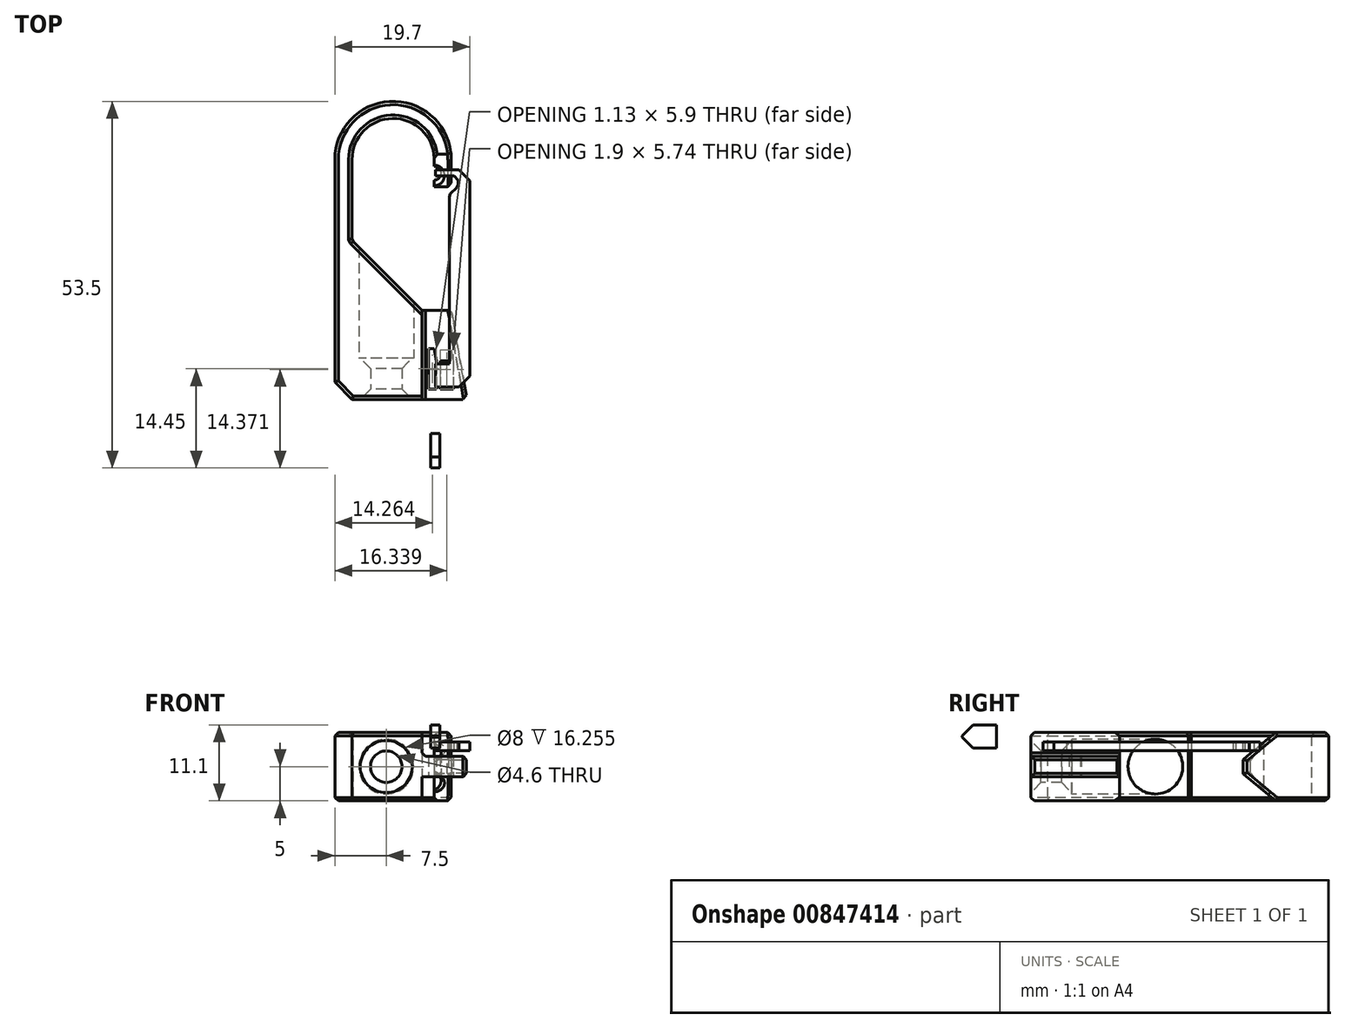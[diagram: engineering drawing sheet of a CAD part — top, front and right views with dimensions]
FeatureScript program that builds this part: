
annotation { "Feature Type Name" : "Feature", "Feature Type Description" : "" }
export const myFeature = defineFeature(function(context is Context, id is Id, definition is map)
    precondition{}
    {
        {
            var Q0;
            Q0=qCreatedBy(makeId("Top.planeOp"),FACE);
            var sketch = newSketch(context, id + "F0", { "sketchPlane" : qUnion([Q0])});
            skCircle(sketch, "E0", {"center": v(-1, -1.5) * mm, "radius": 4 * mm});
            skLineSegment(sketch, "E1.bottom", {"start": v(-8.5, 3.5) * mm, "end": v(8.5, 3.5) * mm});
            skLineSegment(sketch, "E1.top", {"start": v(-8.5, -6.5) * mm, "end": v(8.5, -6.5) * mm});
            skLineSegment(sketch, "E1.left", {"start": v(-8.5, 3.5) * mm, "end": v(-8.5, -6.5) * mm});
            skLineSegment(sketch, "E1.right", {"start": v(8.5, 3.5) * mm, "end": v(8.5, -6.5) * mm});
            skPoint(sketch, "E1.middle", {"position": v(0, -1.5) * mm});
            skCircle(sketch, "E2", {"center": v(-1, -1.5) * mm, "radius": 2.3 * mm});
            skSolve(sketch);
        }
        {
            var Q0;
            Q0=qCreatedBy(makeId("Front.planeOp"),FACE);
            cPlane(context, id + "F1", {"entities" : qUnion([Q0]), "cplaneType" : CPlaneType.OFFSET, "offset" : 3.5 * mm, "oppositeDirection" : true, "width" : 150 * mm, "height" : 150 * mm});
        }
        {
            var Q0;
            Q0=qCreatedBy(id+"F1.planeOp",FACE);
            var sketch = newSketch(context, id + "F2", { "sketchPlane" : qUnion([Q0])});
            skLineSegment(sketch, "E3", {"start": v(0, 0) * mm, "end": v(8.5, 0) * mm});
            skLineSegment(sketch, "E4.MirrorCS", {"start": v(0, 0) * mm, "end": v(-8.5, 0) * mm});
            skLineSegment(sketch, "E5", {"start": v(8.5, 0) * mm, "end": v(8.5, 13) * mm});
            skLineSegment(sketch, "E6", {"start": v(8.5, 13) * mm, "end": v(4.2, 13) * mm});
            skLineSegment(sketch, "E7", {"start": v(4.2, 13) * mm, "end": v(-6, 23.2) * mm});
            skLineSegment(sketch, "E8", {"start": v(-8.5, 0) * mm, "end": v(-8.5, 35) * mm});
            skLineSegment(sketch, "E9", {"start": v(-6, 23.2) * mm, "end": v(-6, 35) * mm});
            skLineSegment(sketch, "E10", {"start": v(-6, 35) * mm, "end": v(0, 35) * mm});
            skArc(sketch, "E11", {"start": v(8.5, 35) * mm, "mid": v(0, 43.5) * mm, "end": v(-8.5, 35) * mm});
            skArc(sketch, "E12", {"start": v(6, 35) * mm, "mid": v(0, 41) * mm, "end": v(-6, 35) * mm});
            skLineSegment(sketch, "E13", {"start": v(0, 35) * mm, "end": v(8.5, 35) * mm});
            skLineSegment(sketch, "E14", {"start": v(6, 35) * mm, "end": v(6, 31) * mm});
            skLineSegment(sketch, "E15.bottom", {"start": v(6, 31) * mm, "end": v(8.5, 31) * mm});
            skLineSegment(sketch, "E15.top", {"start": v(6, 35) * mm, "end": v(8.5, 35) * mm});
            skLineSegment(sketch, "E15.left", {"start": v(6, 31) * mm, "end": v(6, 35) * mm});
            skLineSegment(sketch, "E15.right", {"start": v(8.5, 31) * mm, "end": v(8.5, 35) * mm});
            skLineSegment(sketch, "E16", {"start": v(8.5, 13) * mm, "end": v(10.8, 0) * mm});
            skLineSegment(sketch, "E17", {"start": v(10.8, 0) * mm, "end": v(8.5, 0) * mm});
            skLineSegment(sketch, "E18", {"start": v(4.2, 13) * mm, "end": v(4.2, 0) * mm});
            skLineSegment(sketch, "E19.0", {"start": v(5.2, 12) * mm, "end": v(5.2, 0) * mm});
            skLineSegment(sketch, "E19.1", {"start": v(7.66, 12) * mm, "end": v(5.2, 12) * mm});
            skLineSegment(sketch, "E19.2", {"start": v(7.66, 12) * mm, "end": v(9.6, 1) * mm});
            skLineSegment(sketch, "E19.3", {"start": v(9.6, 1) * mm, "end": v(8.5, 1) * mm});
            skLineSegment(sketch, "E20", {"start": v(8.5, 1) * mm, "end": v(5.2, 1) * mm});
            skLineSegment(sketch, "E21", {"start": v(5.2, 12) * mm, "end": v(7.14, 1) * mm});
            skCircle(sketch, "E22", {"center": v(6, 33) * mm, "radius": 1 * mm});
            skLineSegment(sketch, "E23.0", {"start": v(8.5, 11.5) * mm, "end": v(4.2, 11.5) * mm});
            skLineSegment(sketch, "E24.0", {"start": v(0, 1.5) * mm, "end": v(8.5, 1.5) * mm});
            skLineSegment(sketch, "E24.1", {"start": v(10.8, 1.5) * mm, "end": v(8.5, 1.5) * mm});
            skLineSegment(sketch, "E25", {"start": v(8.79, 5.6) * mm, "end": v(8.79, 1) * mm});
            skLineSegment(sketch, "E26", {"start": v(8.79, 5.6) * mm, "end": v(6.33, 5.6) * mm});
            skLineSegment(sketch, "E27", {"start": v(7.66, 12) * mm, "end": v(7.66, 7.4) * mm});
            skLineSegment(sketch, "E28", {"start": v(7.66, 7.4) * mm, "end": v(5.2, 7.4) * mm});
            skLineSegment(sketch, "E29", {"start": v(6.33, 5.6) * mm, "end": v(6.33, 1) * mm});
            skLineSegment(sketch, "E30", {"start": v(8.79, 5.6) * mm, "end": v(6.89, 5.6) * mm});
            skLineSegment(sketch, "E31", {"start": v(6.89, 5.6) * mm, "end": v(6.89, 1) * mm});
            skLineSegment(sketch, "E32", {"start": v(5.2, 7.4) * mm, "end": v(7.1, 7.4) * mm});
            skLineSegment(sketch, "E33", {"start": v(7.1, 7.4) * mm, "end": v(7.1, 12) * mm});
            skSolve(sketch);
        }
        {
            var Q0;
            {var subQ0=sQuery(id+"F2.wireOp",EDGE,"E20");var subQ1=sQuery(id+"F2.wireOp",EDGE,"E19.0");var subQ2=makeQuery(id+"F2.imprint","INTERSECT",VERTEX,{"derivedFrom":[subQ1,subQ0]});Q0=makeQuery(id+"F2.imprint","IMPRINT",FACE,{"disambiguationData":[TD([[makeQuery(id+"F2.imprint","IMPRINT",EDGE,{"disambiguationData":[TD([[subQ2,1.0]])],"derivedFrom":subQ1}),1.0]])]});}
            var Q1;
            {var subQ1=sQuery(id+"F2.wireOp",EDGE,"E6");Q1=makeQuery(id+"F2.imprint","IMPRINT",FACE,{"disambiguationData":[TD([[makeQuery(id+"F2.imprint","IMPRINT",EDGE,{"derivedFrom":subQ1}),1.0]])]});}
            var Q2;
            {var subQ4=sQuery(id+"F2.wireOp",EDGE,"E23.0");var subQ5=sQuery(id+"F2.wireOp",EDGE,"E18");var subQ6=makeQuery(id+"F2.imprint","INTERSECT",VERTEX,{"derivedFrom":[subQ5,subQ4]});Q2=makeQuery(id+"F2.imprint","IMPRINT",FACE,{"disambiguationData":[TD([[makeQuery(id+"F2.imprint","IMPRINT",EDGE,{"disambiguationData":[TD([[subQ6,-1.0]])],"derivedFrom":subQ5}),1.0]])]});}
            var Q3;
            {var subQ4=sQuery(id+"F2.wireOp",EDGE,"E3");var subQ6=sQuery(id+"F2.wireOp",EDGE,"E18");var subQ7=makeQuery(id+"F2.imprint","INTERSECT",VERTEX,{"derivedFrom":[subQ4,subQ6]});Q3=makeQuery(id+"F2.imprint","IMPRINT",FACE,{"disambiguationData":[TD([[makeQuery(id+"F2.imprint","IMPRINT",EDGE,{"disambiguationData":[TD([[subQ7,-1.0]])],"derivedFrom":subQ4}),1.0]])]});}
            var Q4;
            {var subQ4=sQuery(id+"F2.wireOp",EDGE,"E19.0");var subQ5=sQuery(id+"F2.wireOp",EDGE,"E3");var subQ6=makeQuery(id+"F2.imprint","INTERSECT",VERTEX,{"derivedFrom":[subQ5,subQ4]});Q4=makeQuery(id+"F2.imprint","IMPRINT",FACE,{"disambiguationData":[TD([[makeQuery(id+"F2.imprint","IMPRINT",EDGE,{"disambiguationData":[TD([[subQ6,1.0]])],"derivedFrom":subQ4}),1.0]])]});}
            var Q5;
            {var subQ5=sQuery(id+"F2.wireOp",EDGE,"E17");Q5=makeQuery(id+"F2.imprint","IMPRINT",FACE,{"disambiguationData":[TD([[makeQuery(id+"F2.imprint","IMPRINT",EDGE,{"derivedFrom":subQ5}),-1.0]])]});}
            var Q6;
            {var subQ2=sQuery(id+"F2.wireOp",EDGE,"E5");var subQ8=makeQuery(id+"F2.imprint","INTERSECT",VERTEX,{"derivedFrom":[subQ2,sQuery(id+"F2.wireOp",EDGE,"E23.0")]});Q6=makeQuery(id+"F2.imprint","IMPRINT",FACE,{"disambiguationData":[TD([[makeQuery(id+"F2.imprint","IMPRINT",EDGE,{"disambiguationData":[TD([[subQ8,1.0]])],"derivedFrom":subQ2}),-1.0]])]});}
            var Q7;
            {var subQ4=sQuery(id+"F2.wireOp",EDGE,"E4.MirrorCS");Q7=makeQuery(id+"F2.imprint","IMPRINT",FACE,{"disambiguationData":[TD([[makeQuery(id+"F2.imprint","IMPRINT",EDGE,{"derivedFrom":subQ4}),-1.0]])]});}
            var Q8;
            {var subQ0=sQuery(id+"F2.wireOp",EDGE,"E23.0");var subQ1=sQuery(id+"F2.wireOp",EDGE,"E5");var subQ2=makeQuery(id+"F2.imprint","INTERSECT",VERTEX,{"derivedFrom":[subQ1,subQ0]});Q8=makeQuery(id+"F2.imprint","IMPRINT",FACE,{"disambiguationData":[TD([[makeQuery(id+"F2.imprint","IMPRINT",EDGE,{"disambiguationData":[TD([[subQ2,1.0]])],"derivedFrom":subQ1}),1.0]])]});}
            var Q9;
            {var subQ1=sQuery(id+"F2.wireOp",EDGE,"E19.2");var subQ3=sQuery(id+"F2.wireOp",EDGE,"E23.0");var subQ4=makeQuery(id+"F2.imprint","INTERSECT",VERTEX,{"derivedFrom":[subQ1,subQ3]});Q9=makeQuery(id+"F2.imprint","IMPRINT",FACE,{"disambiguationData":[TD([[makeQuery(id+"F2.imprint","IMPRINT",EDGE,{"disambiguationData":[TD([[subQ4,-1.0]])],"derivedFrom":subQ3}),-1.0]])]});}
            var Q10;
            {var subQ5=sQuery(id+"F2.wireOp",EDGE,"E15.bottom");Q10=makeQuery(id+"F2.imprint","IMPRINT",FACE,{"disambiguationData":[TD([[makeQuery(id+"F2.imprint","IMPRINT",EDGE,{"derivedFrom":subQ5}),1.0]])]});}
            var Q11;
            {var subQ1=sQuery(id+"F2.wireOp",EDGE,"E19.2");var subQ3=sQuery(id+"F2.wireOp",EDGE,"E24.1");var subQ4=makeQuery(id+"F2.imprint","INTERSECT",VERTEX,{"derivedFrom":[subQ1,subQ3]});Q11=makeQuery(id+"F2.imprint","IMPRINT",FACE,{"disambiguationData":[TD([[makeQuery(id+"F2.imprint","IMPRINT",EDGE,{"disambiguationData":[TD([[subQ4,-1.0]])],"derivedFrom":subQ3}),-1.0]])]});}
            var Q12;
            {var subQ0=sQuery(id+"F2.wireOp",EDGE,"E19.3");var subQ1=sQuery(id+"F2.wireOp",EDGE,"E19.2");var subQ2=makeQuery(id+"F2.imprint","INTERSECT",VERTEX,{"derivedFrom":[subQ1,subQ0]});Q12=makeQuery(id+"F2.imprint","IMPRINT",FACE,{"disambiguationData":[TD([[makeQuery(id+"F2.imprint","IMPRINT",EDGE,{"disambiguationData":[TD([[subQ2,1.0]])],"derivedFrom":subQ1}),-1.0]])]});}
            var Q13;
            {var subQ0=sQuery(id+"F2.wireOp",EDGE,"E21");var subQ1=sQuery(id+"F2.wireOp",EDGE,"E20");var subQ2=makeQuery(id+"F2.imprint","INTERSECT",VERTEX,{"derivedFrom":[subQ1,subQ0]});Q13=makeQuery(id+"F2.imprint","IMPRINT",FACE,{"disambiguationData":[TD([[makeQuery(id+"F2.imprint","IMPRINT",EDGE,{"disambiguationData":[TD([[subQ2,-1.0]])],"derivedFrom":subQ1}),-1.0]])]});}
            var Q14;
            {var subQ0=sQuery(id+"F2.wireOp",EDGE,"E20");var subQ5=sQuery(id+"F2.wireOp",EDGE,"E21");var subQ6=makeQuery(id+"F2.imprint","INTERSECT",VERTEX,{"derivedFrom":[subQ0,subQ5]});Q14=makeQuery(id+"F2.imprint","IMPRINT",FACE,{"disambiguationData":[TD([[makeQuery(id+"F2.imprint","IMPRINT",EDGE,{"disambiguationData":[TD([[subQ6,1.0]])],"derivedFrom":subQ5}),1.0]])]});}
            var Q15;
            {var subQ0=sQuery(id+"F2.wireOp",EDGE,"E19.3");var subQ5=sQuery(id+"F2.wireOp",EDGE,"E25");var subQ6=makeQuery(id+"F2.imprint","INTERSECT",VERTEX,{"derivedFrom":[subQ0,subQ5]});Q15=makeQuery(id+"F2.imprint","IMPRINT",FACE,{"disambiguationData":[TD([[makeQuery(id+"F2.imprint","IMPRINT",EDGE,{"disambiguationData":[TD([[subQ6,1.0]])],"derivedFrom":subQ5}),-1.0]])]});}
            var Q16;
            {var subQ0=sQuery(id+"F2.wireOp",EDGE,"E27");var subQ5=sQuery(id+"F2.wireOp",EDGE,"E23.0");var subQ6=makeQuery(id+"F2.imprint","INTERSECT",VERTEX,{"derivedFrom":[subQ5,subQ0]});Q16=makeQuery(id+"F2.imprint","IMPRINT",FACE,{"disambiguationData":[TD([[makeQuery(id+"F2.imprint","IMPRINT",EDGE,{"disambiguationData":[TD([[subQ6,-1.0]])],"derivedFrom":subQ5}),-1.0]])]});}
            var Q17;
            {var subQ0=sQuery(id+"F2.wireOp",EDGE,"E21");var subQ5=sQuery(id+"F2.wireOp",EDGE,"E23.0");var subQ7=makeQuery(id+"F2.imprint","INTERSECT",VERTEX,{"derivedFrom":[subQ0,subQ5]});Q17=makeQuery(id+"F2.imprint","IMPRINT",FACE,{"disambiguationData":[TD([[makeQuery(id+"F2.imprint","IMPRINT",EDGE,{"disambiguationData":[TD([[subQ7,1.0]])],"derivedFrom":subQ5}),-1.0]])]});}
            var Q18;
            {var subQ1=sQuery(id+"F2.wireOp",EDGE,"E19.0");var subQ3=sQuery(id+"F2.wireOp",EDGE,"E23.0");var subQ4=makeQuery(id+"F2.imprint","INTERSECT",VERTEX,{"derivedFrom":[subQ1,subQ3]});Q18=makeQuery(id+"F2.imprint","IMPRINT",FACE,{"disambiguationData":[TD([[makeQuery(id+"F2.imprint","IMPRINT",EDGE,{"disambiguationData":[TD([[subQ4,1.0]])],"derivedFrom":subQ3}),-1.0]])]});}
            var Q19;
            {var subQ5=sQuery(id+"F2.wireOp",EDGE,"E28");Q19=makeQuery(id+"F2.imprint","IMPRINT",FACE,{"disambiguationData":[TD([[makeQuery(id+"F2.imprint","IMPRINT",EDGE,{"derivedFrom":subQ5}),-1.0]])]});}
            var Q20;
            {var subQ0=sQuery(id+"F2.wireOp",EDGE,"E26");Q20=makeQuery(id+"F2.imprint","IMPRINT",FACE,{"disambiguationData":[TD([[makeQuery(id+"F2.imprint","IMPRINT",EDGE,{"derivedFrom":subQ0}),-1.0]])]});}
            var Q21;
            {var subQ5=sQuery(id+"F2.wireOp",EDGE,"E32");var subQ6=sQuery(id+"F2.wireOp",EDGE,"E19.0");var subQ7=makeQuery(id+"F2.imprint","INTERSECT",VERTEX,{"derivedFrom":[subQ6,subQ5]});Q21=makeQuery(id+"F2.imprint","IMPRINT",FACE,{"disambiguationData":[TD([[makeQuery(id+"F2.imprint","IMPRINT",EDGE,{"disambiguationData":[TD([[subQ7,-1.0]])],"derivedFrom":subQ6}),1.0]])]});}
            var Q22;
            {var subQ0=sQuery(id+"F2.wireOp",EDGE,"E26");Q22=makeQuery(id+"F2.imprint","IMPRINT",FACE,{"disambiguationData":[TD([[makeQuery(id+"F2.imprint","IMPRINT",EDGE,{"derivedFrom":subQ0}),1.0]])]});}
            var Q23;
            {var subQ0=sQuery(id+"F2.wireOp",EDGE,"E29");var subQ5=sQuery(id+"F2.wireOp",EDGE,"E24.0");var subQ6=makeQuery(id+"F2.imprint","INTERSECT",VERTEX,{"derivedFrom":[subQ5,subQ0]});Q23=makeQuery(id+"F2.imprint","IMPRINT",FACE,{"disambiguationData":[TD([[makeQuery(id+"F2.imprint","IMPRINT",EDGE,{"disambiguationData":[TD([[subQ6,-1.0]])],"derivedFrom":subQ5}),1.0]])]});}
            var Q24;
            {var subQ0=sQuery(id+"F2.wireOp",EDGE,"E29");var subQ1=sQuery(id+"F2.wireOp",EDGE,"E20");var subQ2=makeQuery(id+"F2.imprint","INTERSECT",VERTEX,{"derivedFrom":[subQ1,subQ0]});Q24=makeQuery(id+"F2.imprint","IMPRINT",FACE,{"disambiguationData":[TD([[makeQuery(id+"F2.imprint","IMPRINT",EDGE,{"disambiguationData":[TD([[subQ2,1.0]])],"derivedFrom":subQ1}),-1.0]])]});}
            var Q25;
            {var subQ0=sQuery(id+"F2.wireOp",EDGE,"E30");var subQ1=sQuery(id+"F2.wireOp",EDGE,"E5");var subQ2=makeQuery(id+"F2.imprint","INTERSECT",VERTEX,{"derivedFrom":[subQ1,subQ0]});Q25=makeQuery(id+"F2.imprint","IMPRINT",FACE,{"disambiguationData":[TD([[makeQuery(id+"F2.imprint","IMPRINT",EDGE,{"disambiguationData":[TD([[subQ2,-1.0]])],"derivedFrom":subQ1}),-1.0]])]});}
            extrude(context, id + "F3", {"entities" : qUnion([Q0, Q1, Q2, Q3, Q4, Q5, Q6, Q7, Q8, Q9, Q10, Q11, Q12, Q13, Q14, Q15, Q16, Q17, Q18, Q19, Q20, Q21, Q22, Q23, Q24, Q25]), "depth" : 10 * mm, "offsetDistance" : 25 * mm});
        }
        {
            var Q0;
            Q0=makeQuery(id+"F0.imprint","IMPRINT",FACE,{"disambiguationData":[TD([[makeQuery(id+"F0.imprint","IMPRINT",EDGE,{"derivedFrom":sQuery(id+"F0.wireOp",EDGE,"E0")}),1.0]])]});
            var Q1;
            Q1=makeQuery(id+"F0.imprint","IMPRINT",FACE,{"disambiguationData":[TD([[makeQuery(id+"F0.imprint","IMPRINT",EDGE,{"derivedFrom":sQuery(id+"F0.wireOp",EDGE,"E2")}),1.0]])]});
            extrude(context, id + "F4", {"entities" : qUnion([Q0, Q1]), "operationType" : NewBodyOperationType.REMOVE, "depth" : 25 * mm, "offsetDistance" : 25 * mm});
        }
        {
            var Q0;
            Q0=makeQuery(id+"F0.imprint","IMPRINT",FACE,{"disambiguationData":[TD([[makeQuery(id+"F0.imprint","IMPRINT",EDGE,{"derivedFrom":sQuery(id+"F0.wireOp",EDGE,"E0")}),1.0]])]});
            extrude(context, id + "F5", {"entities" : qUnion([Q0]), "operationType" : NewBodyOperationType.ADD, "depth" : 6 * mm, "offsetDistance" : 25 * mm});
        }
        {
            var Q0;
            Q0=makeQuery(id+"F3.opExtrude","CAP_EDGE",EDGE,{"disambiguationData":[OSD([sQuery(id+"F2.wireOp",EDGE,"E15.bottom")])],"isStart":false});
            var Q1;
            Q1=makeQuery(id+"F3.opExtrude","CAP_EDGE",EDGE,{"disambiguationData":[OSD([sQuery(id+"F2.wireOp",EDGE,"E15.bottom")])],"isStart":true});
            chamfer(context, id + "F6", {"entities" : qUnion([Q0, Q1]), "chamferType" : ChamferType.OFFSET_ANGLE, "width" : 4 * mm, "oppositeDirection" : true, "angle" : 50 * degree, "tangentPropagation" : true});
        }
        {
            var Q0;
            Q0=makeQuery(id+"F3.opExtrude","SWEPT_EDGE",EDGE,{"disambiguationData":[OSD([sQuery(id+"F2.wireOp",EDGE,"E4.MirrorCS"),sQuery(id+"F2.wireOp",EDGE,"E8")])]});
            chamfer(context, id + "F7", {"entities" : qUnion([Q0]), "width" : 2.5 * mm, "tangentPropagation" : true});
        }
        {
            var Q0;
            Q0=makeQuery(id+"F5.opExtrude","CAP_EDGE",EDGE,{"disambiguationData":[OSD([sQuery(id+"F0.wireOp",EDGE,"E2")])],"isStart":true});
            var Q1;
            Q1=makeQuery(id+"F5.opExtrude","CAP_EDGE",EDGE,{"disambiguationData":[OSD([sQuery(id+"F0.wireOp",EDGE,"E2")])],"isStart":false});
            chamfer(context, id + "F8", {"entities" : qUnion([Q0, Q1]), "width" : 1.5 * mm, "tangentPropagation" : true});
        }
        {
            var Q0;
            Q0=makeQuery(id+"F3.opExtrude","SWEPT_EDGE",EDGE,{"disambiguationData":[OSD([sQuery(id+"F2.wireOp",EDGE,"E7"),sQuery(id+"F2.wireOp",EDGE,"E9")])]});
            var Q1;
            Q1=makeQuery(id+"F3.opExtrude","SWEPT_EDGE",EDGE,{"disambiguationData":[OSD([sQuery(id+"F2.wireOp",EDGE,"E15.bottom"),sQuery(id+"F2.wireOp",EDGE,"E15.right")])]});
            chamfer(context, id + "F9", {"entities" : qUnion([Q0, Q1]), "width" : .6 * mm, "tangentPropagation" : true});
        }
        {
            var Q0;
            Q0=qCreatedBy(id+"F1.planeOp",FACE);
            var sketch = newSketch(context, id + "F10", { "sketchPlane" : qUnion([Q0])});
            skLineSegment(sketch, "E34", {"start": v(0, 0) * mm, "end": v(4.2, 0) * mm});
            skLineSegment(sketch, "E35", {"start": v(4.2, 0) * mm, "end": v(11.2, 0) * mm});
            skLineSegment(sketch, "E36", {"start": v(4.2, 0) * mm, "end": v(4.2, 15.17) * mm});
            skLineSegment(sketch, "E37.bottom", {"start": v(4.2, 15.17) * mm, "end": v(11.2, 15.17) * mm});
            skLineSegment(sketch, "E37.left", {"start": v(4.2, 15.17) * mm, "end": v(4.2, 0) * mm});
            skLineSegment(sketch, "E37.right", {"start": v(11.2, 15.17) * mm, "end": v(11.2, 0) * mm});
            skSolve(sketch);
        }
        {
            var Q0;
            Q0=qSketchRegion(id+"F10",true);
            extrude(context, id + "F11", {"entities" : qUnion([Q0]), "operationType" : NewBodyOperationType.REMOVE, "depth" : 3.5 * mm, "offsetDistance" : 25 * mm});
        }
        {
            var Q0;
            Q0=qCreatedBy(id+"F1.planeOp",FACE);
            cPlane(context, id + "F12", {"entities" : qUnion([Q0]), "cplaneType" : CPlaneType.OFFSET, "offset" : 10 * mm, "width" : 150 * mm, "height" : 150 * mm});
        }
        {
            var Q0;
            Q0=qCreatedBy(id+"F12.planeOp",FACE);
            var sketch = newSketch(context, id + "F13", { "sketchPlane" : qUnion([Q0])});
            skLineSegment(sketch, "E38", {"start": v(0, 0) * mm, "end": v(4.2, 0) * mm});
            skLineSegment(sketch, "E39", {"start": v(4.2, 0) * mm, "end": v(11.2, 0) * mm});
            skLineSegment(sketch, "E40", {"start": v(11.2, 0) * mm, "end": v(11.2, 14.54) * mm});
            skLineSegment(sketch, "E41.bottom", {"start": v(11.2, 14.54) * mm, "end": v(4.2, 14.54) * mm});
            skLineSegment(sketch, "E41.top", {"start": v(11.2, 0) * mm, "end": v(4.2, 0) * mm});
            skLineSegment(sketch, "E41.left", {"start": v(11.2, 14.54) * mm, "end": v(11.2, 0) * mm});
            skLineSegment(sketch, "E41.right", {"start": v(4.2, 14.54) * mm, "end": v(4.2, 0) * mm});
            skSolve(sketch);
        }
        {
            var Q0;
            Q0=qSketchRegion(id+"F13",true);
            extrude(context, id + "F14", {"entities" : qUnion([Q0]), "operationType" : NewBodyOperationType.REMOVE, "oppositeDirection" : true, "depth" : 3.5 * mm, "offsetDistance" : 25 * mm});
        }
        {
            var Q0;
            Q0=makeQuery(id+"F14.boolean.opBoolean","INTERSECT",EDGE,{"derivedFrom":[makeQuery(id+"F3.opExtrude","SWEPT_FACE",FACE,{"disambiguationData":[OSD([sQuery(id+"F2.wireOp",EDGE,"E16")])]}),makeQuery(id+"F14.opExtrude","CAP_FACE",FACE,{"disambiguationData":[OSD([sQuery(id+"F13.wireOp",EDGE,"E41.bottom"),sQuery(id+"F13.wireOp",EDGE,"E41.top"),sQuery(id+"F13.wireOp",EDGE,"E41.left"),sQuery(id+"F13.wireOp",EDGE,"E41.right")])],"isStart":false})]});
            var Q1;
            Q1=makeQuery(id+"F11.boolean.opBoolean","INTERSECT",EDGE,{"derivedFrom":[makeQuery(id+"F3.opExtrude","SWEPT_FACE",FACE,{"disambiguationData":[OSD([sQuery(id+"F2.wireOp",EDGE,"E16")])]}),makeQuery(id+"F11.opExtrude","CAP_FACE",FACE,{"disambiguationData":[OSD([sQuery(id+"F10.wireOp",EDGE,"E37.bottom"),sQuery(id+"F10.wireOp",EDGE,"E35"),sQuery(id+"F10.wireOp",EDGE,"E37.left"),sQuery(id+"F10.wireOp",EDGE,"E37.right")])],"isStart":false})]});
            var Q2;
            Q2=makeQuery(id+"F3.opExtrude","CAP_EDGE",EDGE,{"disambiguationData":[OSD([sQuery(id+"F2.wireOp",EDGE,"E8")])],"isStart":false});
            var Q3;
            Q3=makeQuery(id+"F3.opExtrude","CAP_EDGE",EDGE,{"disambiguationData":[OSD([sQuery(id+"F2.wireOp",EDGE,"E8")])],"isStart":true});
            var Q4;
            Q4=makeQuery(id+"F3.opExtrude","CAP_EDGE",EDGE,{"disambiguationData":[OSD([sQuery(id+"F2.wireOp",EDGE,"E9")])],"isStart":true});
            var Q5;
            Q5=makeQuery(id+"F3.opExtrude","CAP_EDGE",EDGE,{"disambiguationData":[OSD([sQuery(id+"F2.wireOp",EDGE,"E9")])],"isStart":false});
            var Q6;
            Q6=makeQuery(id+"F3.opExtrude","CAP_EDGE",EDGE,{"disambiguationData":[OSD([sQuery(id+"F2.wireOp",EDGE,"E7")])],"isStart":false});
            var Q7;
            Q7=makeQuery(id+"F3.opExtrude","CAP_EDGE",EDGE,{"disambiguationData":[OSD([sQuery(id+"F2.wireOp",EDGE,"E7")])],"isStart":true});
            var Q8;
            {var subQ0=sQuery(id+"F2.wireOp",EDGE,"E9");var subQ1=sQuery(id+"F2.wireOp",EDGE,"E7");Q8=makeQuery(id+"F9.opChamfer","BLEND_EDGE",EDGE,{"blendedFrom":[makeQuery(id+"F3.opExtrude","SWEPT_EDGE",EDGE,{"disambiguationData":[OSD([subQ1,subQ0])]}),makeQuery(id+"F3.opExtrude","CAP_FACE",FACE,{"disambiguationData":[OSD([sQuery(id+"F2.wireOp",EDGE,"E3"),sQuery(id+"F2.wireOp",EDGE,"E4.MirrorCS"),sQuery(id+"F2.wireOp",EDGE,"E6"),subQ1,sQuery(id+"F2.wireOp",EDGE,"E8"),subQ0,sQuery(id+"F2.wireOp",EDGE,"E11"),sQuery(id+"F2.wireOp",EDGE,"E12"),sQuery(id+"F2.wireOp",EDGE,"E15.bottom"),sQuery(id+"F2.wireOp",EDGE,"E15.left"),sQuery(id+"F2.wireOp",EDGE,"E15.right"),sQuery(id+"F2.wireOp",EDGE,"UHZCBOe5-mY96-04BQ-GKVw-0XouIqEKjYRg"),sQuery(id+"F2.wireOp",EDGE,"E16"),sQuery(id+"F2.wireOp",EDGE,"E17")])],"isStart":true})],"blendedInto":[makeQuery(id+"F3.opExtrude","CAP_FACE",FACE,{"disambiguationData":[OSD([sQuery(id+"F2.wireOp",EDGE,"E3"),sQuery(id+"F2.wireOp",EDGE,"E4.MirrorCS"),sQuery(id+"F2.wireOp",EDGE,"E6"),subQ1,sQuery(id+"F2.wireOp",EDGE,"E8"),subQ0,sQuery(id+"F2.wireOp",EDGE,"E11"),sQuery(id+"F2.wireOp",EDGE,"E12"),sQuery(id+"F2.wireOp",EDGE,"E15.bottom"),sQuery(id+"F2.wireOp",EDGE,"E15.left"),sQuery(id+"F2.wireOp",EDGE,"E15.right"),sQuery(id+"F2.wireOp",EDGE,"UHZCBOe5-mY96-04BQ-GKVw-0XouIqEKjYRg"),sQuery(id+"F2.wireOp",EDGE,"E16"),sQuery(id+"F2.wireOp",EDGE,"E17")])],"isStart":true})]});}
            var Q9;
            {var subQ0=sQuery(id+"F2.wireOp",EDGE,"E9");var subQ1=sQuery(id+"F2.wireOp",EDGE,"E7");Q9=makeQuery(id+"F9.opChamfer","BLEND_EDGE",EDGE,{"blendedFrom":[makeQuery(id+"F3.opExtrude","SWEPT_EDGE",EDGE,{"disambiguationData":[OSD([subQ1,subQ0])]}),makeQuery(id+"F3.opExtrude","CAP_FACE",FACE,{"disambiguationData":[OSD([sQuery(id+"F2.wireOp",EDGE,"E3"),sQuery(id+"F2.wireOp",EDGE,"E4.MirrorCS"),sQuery(id+"F2.wireOp",EDGE,"E6"),subQ1,sQuery(id+"F2.wireOp",EDGE,"E8"),subQ0,sQuery(id+"F2.wireOp",EDGE,"E11"),sQuery(id+"F2.wireOp",EDGE,"E12"),sQuery(id+"F2.wireOp",EDGE,"E15.bottom"),sQuery(id+"F2.wireOp",EDGE,"E15.left"),sQuery(id+"F2.wireOp",EDGE,"E15.right"),sQuery(id+"F2.wireOp",EDGE,"UHZCBOe5-mY96-04BQ-GKVw-0XouIqEKjYRg"),sQuery(id+"F2.wireOp",EDGE,"E16"),sQuery(id+"F2.wireOp",EDGE,"E17")])],"isStart":false})],"blendedInto":[makeQuery(id+"F3.opExtrude","CAP_FACE",FACE,{"disambiguationData":[OSD([sQuery(id+"F2.wireOp",EDGE,"E3"),sQuery(id+"F2.wireOp",EDGE,"E4.MirrorCS"),sQuery(id+"F2.wireOp",EDGE,"E6"),subQ1,sQuery(id+"F2.wireOp",EDGE,"E8"),subQ0,sQuery(id+"F2.wireOp",EDGE,"E11"),sQuery(id+"F2.wireOp",EDGE,"E12"),sQuery(id+"F2.wireOp",EDGE,"E15.bottom"),sQuery(id+"F2.wireOp",EDGE,"E15.left"),sQuery(id+"F2.wireOp",EDGE,"E15.right"),sQuery(id+"F2.wireOp",EDGE,"UHZCBOe5-mY96-04BQ-GKVw-0XouIqEKjYRg"),sQuery(id+"F2.wireOp",EDGE,"E16"),sQuery(id+"F2.wireOp",EDGE,"E17")])],"isStart":false})]});}
            var Q10;
            Q10=makeQuery(id+"F6.opChamfer","BLEND_EDGE",EDGE,{"blendedFrom":[makeQuery(id+"F3.opExtrude","CAP_EDGE",EDGE,{"disambiguationData":[OSD([sQuery(id+"F2.wireOp",EDGE,"E15.bottom")])],"isStart":false}),makeQuery(id+"F3.opExtrude","SWEPT_FACE",FACE,{"disambiguationData":[OSD([sQuery(id+"F2.wireOp",EDGE,"E15.left")])]})],"blendedInto":[makeQuery(id+"F3.opExtrude","SWEPT_FACE",FACE,{"disambiguationData":[OSD([sQuery(id+"F2.wireOp",EDGE,"E15.left")])]})]});
            var Q11;
            Q11=makeQuery(id+"F6.opChamfer","BLEND_EDGE",EDGE,{"blendedFrom":[makeQuery(id+"F3.opExtrude","CAP_EDGE",EDGE,{"disambiguationData":[OSD([sQuery(id+"F2.wireOp",EDGE,"E15.bottom")])],"isStart":true}),makeQuery(id+"F3.opExtrude","SWEPT_FACE",FACE,{"disambiguationData":[OSD([sQuery(id+"F2.wireOp",EDGE,"E15.left")])]})],"blendedInto":[makeQuery(id+"F3.opExtrude","SWEPT_FACE",FACE,{"disambiguationData":[OSD([sQuery(id+"F2.wireOp",EDGE,"E15.left")])]})]});
            var Q12;
            {var subQ0=sQuery(id+"F2.wireOp",EDGE,"E15.right");Q12=makeQuery(id+"F6.opChamfer","BLEND_EDGE",EDGE,{"blendedFrom":[makeQuery(id+"F3.opExtrude","CAP_EDGE",EDGE,{"disambiguationData":[OSD([sQuery(id+"F2.wireOp",EDGE,"E15.bottom")])],"isStart":false}),makeQuery(id+"F3.opExtrude","SWEPT_FACE",FACE,{"disambiguationData":[OSD([subQ0]),TDD([makeQuery(id+"F2.imprint","IMPRINT",EDGE,{"disambiguationData":[TD([[makeQuery(id+"F2.imprint","INTERSECT",VERTEX,{"disambiguationData":[OD(1.0)],"derivedFrom":[subQ0,sQuery(id+"F2.wireOp",EDGE,"UHZCBOe5-mY96-04BQ-GKVw-0XouIqEKjYRg")]}),-1.0]])],"derivedFrom":subQ0})])]})],"blendedInto":[makeQuery(id+"F3.opExtrude","SWEPT_FACE",FACE,{"disambiguationData":[OSD([subQ0]),TDD([makeQuery(id+"F2.imprint","IMPRINT",EDGE,{"disambiguationData":[TD([[makeQuery(id+"F2.imprint","INTERSECT",VERTEX,{"disambiguationData":[OD(1.0)],"derivedFrom":[subQ0,sQuery(id+"F2.wireOp",EDGE,"UHZCBOe5-mY96-04BQ-GKVw-0XouIqEKjYRg")]}),-1.0]])],"derivedFrom":subQ0})])]})]});}
            var Q13;
            Q13=makeQuery(id+"F6.opChamfer","BLEND_EDGE",EDGE,{"blendedFrom":[makeQuery(id+"F3.opExtrude","CAP_EDGE",EDGE,{"disambiguationData":[OSD([sQuery(id+"F2.wireOp",EDGE,"E15.bottom")])],"isStart":false}),makeQuery(id+"F3.opExtrude","SWEPT_FACE",FACE,{"disambiguationData":[OSD([sQuery(id+"F2.wireOp",EDGE,"UHZCBOe5-mY96-04BQ-GKVw-0XouIqEKjYRg")])]})],"blendedInto":[makeQuery(id+"F3.opExtrude","SWEPT_FACE",FACE,{"disambiguationData":[OSD([sQuery(id+"F2.wireOp",EDGE,"UHZCBOe5-mY96-04BQ-GKVw-0XouIqEKjYRg")])]})]});
            var Q14;
            {var subQ0=sQuery(id+"F2.wireOp",EDGE,"E15.right");var subQ1=sQuery(id+"F2.wireOp",EDGE,"E15.bottom");Q14=makeQuery(id+"F6.opChamfer","BLEND_EDGE",EDGE,{"blendedFrom":[makeQuery(id+"F3.opExtrude","CAP_EDGE",EDGE,{"disambiguationData":[OSD([subQ1])],"isStart":false}),makeQuery(id+"F3.opExtrude","SWEPT_FACE",FACE,{"disambiguationData":[OSD([subQ0]),TDD([makeQuery(id+"F2.imprint","IMPRINT",EDGE,{"disambiguationData":[TD([[makeQuery(id+"F2.imprint","INTERSECT",VERTEX,{"derivedFrom":[subQ1,subQ0]}),-1.0]])],"derivedFrom":subQ0})])]})],"blendedInto":[makeQuery(id+"F3.opExtrude","SWEPT_FACE",FACE,{"disambiguationData":[OSD([subQ0]),TDD([makeQuery(id+"F2.imprint","IMPRINT",EDGE,{"disambiguationData":[TD([[makeQuery(id+"F2.imprint","INTERSECT",VERTEX,{"derivedFrom":[subQ1,subQ0]}),-1.0]])],"derivedFrom":subQ0})])]})]});}
            var Q15;
            {var subQ0=sQuery(id+"F2.wireOp",EDGE,"E15.right");Q15=makeQuery(id+"F6.opChamfer","BLEND_EDGE",EDGE,{"blendedFrom":[makeQuery(id+"F3.opExtrude","CAP_EDGE",EDGE,{"disambiguationData":[OSD([sQuery(id+"F2.wireOp",EDGE,"E15.bottom")])],"isStart":true}),makeQuery(id+"F3.opExtrude","SWEPT_FACE",FACE,{"disambiguationData":[OSD([subQ0]),TDD([makeQuery(id+"F2.imprint","IMPRINT",EDGE,{"disambiguationData":[TD([[makeQuery(id+"F2.imprint","INTERSECT",VERTEX,{"disambiguationData":[OD(1.0)],"derivedFrom":[subQ0,sQuery(id+"F2.wireOp",EDGE,"UHZCBOe5-mY96-04BQ-GKVw-0XouIqEKjYRg")]}),-1.0]])],"derivedFrom":subQ0})])]})],"blendedInto":[makeQuery(id+"F3.opExtrude","SWEPT_FACE",FACE,{"disambiguationData":[OSD([subQ0]),TDD([makeQuery(id+"F2.imprint","IMPRINT",EDGE,{"disambiguationData":[TD([[makeQuery(id+"F2.imprint","INTERSECT",VERTEX,{"disambiguationData":[OD(1.0)],"derivedFrom":[subQ0,sQuery(id+"F2.wireOp",EDGE,"UHZCBOe5-mY96-04BQ-GKVw-0XouIqEKjYRg")]}),-1.0]])],"derivedFrom":subQ0})])]})]});}
            var Q16;
            Q16=makeQuery(id+"F6.opChamfer","BLEND_EDGE",EDGE,{"blendedFrom":[makeQuery(id+"F3.opExtrude","CAP_EDGE",EDGE,{"disambiguationData":[OSD([sQuery(id+"F2.wireOp",EDGE,"E15.bottom")])],"isStart":true}),makeQuery(id+"F3.opExtrude","SWEPT_FACE",FACE,{"disambiguationData":[OSD([sQuery(id+"F2.wireOp",EDGE,"UHZCBOe5-mY96-04BQ-GKVw-0XouIqEKjYRg")])]})],"blendedInto":[makeQuery(id+"F3.opExtrude","SWEPT_FACE",FACE,{"disambiguationData":[OSD([sQuery(id+"F2.wireOp",EDGE,"UHZCBOe5-mY96-04BQ-GKVw-0XouIqEKjYRg")])]})]});
            var Q17;
            {var subQ0=sQuery(id+"F2.wireOp",EDGE,"E15.right");var subQ1=sQuery(id+"F2.wireOp",EDGE,"E15.bottom");Q17=makeQuery(id+"F6.opChamfer","BLEND_EDGE",EDGE,{"blendedFrom":[makeQuery(id+"F3.opExtrude","CAP_EDGE",EDGE,{"disambiguationData":[OSD([subQ1])],"isStart":true}),makeQuery(id+"F3.opExtrude","SWEPT_FACE",FACE,{"disambiguationData":[OSD([subQ0]),TDD([makeQuery(id+"F2.imprint","IMPRINT",EDGE,{"disambiguationData":[TD([[makeQuery(id+"F2.imprint","INTERSECT",VERTEX,{"derivedFrom":[subQ1,subQ0]}),-1.0]])],"derivedFrom":subQ0})])]})],"blendedInto":[makeQuery(id+"F3.opExtrude","SWEPT_FACE",FACE,{"disambiguationData":[OSD([subQ0]),TDD([makeQuery(id+"F2.imprint","IMPRINT",EDGE,{"disambiguationData":[TD([[makeQuery(id+"F2.imprint","INTERSECT",VERTEX,{"derivedFrom":[subQ1,subQ0]}),-1.0]])],"derivedFrom":subQ0})])]})]});}
            var Q18;
            Q18=makeQuery(id+"F11.boolean.opBoolean","COPY",EDGE,{"derivedFrom":makeQuery(id+"F11.opExtrude","CAP_EDGE",EDGE,{"disambiguationData":[OSD([sQuery(id+"F10.wireOp",EDGE,"E37.left")])],"isStart":true})});
            var Q19;
            Q19=makeQuery(id+"F14.boolean.opBoolean","COPY",EDGE,{"derivedFrom":makeQuery(id+"F14.opExtrude","CAP_EDGE",EDGE,{"disambiguationData":[OSD([sQuery(id+"F13.wireOp",EDGE,"E41.right")])],"isStart":true})});
            var Q20;
            Q20=makeQuery(id+"F14.boolean.opBoolean","COPY",EDGE,{"derivedFrom":makeQuery(id+"F14.opExtrude","CAP_EDGE",EDGE,{"disambiguationData":[OSD([sQuery(id+"F13.wireOp",EDGE,"E41.right")])],"isStart":false})});
            var Q21;
            Q21=makeQuery(id+"F11.boolean.opBoolean","COPY",EDGE,{"derivedFrom":makeQuery(id+"F11.opExtrude","CAP_EDGE",EDGE,{"disambiguationData":[OSD([sQuery(id+"F10.wireOp",EDGE,"E37.left")])],"isStart":false})});
            var Q22;
            Q22=makeQuery(id+"F3.opExtrude","SWEPT_EDGE",EDGE,{"disambiguationData":[OSD([sQuery(id+"F2.wireOp",EDGE,"E5"),sQuery(id+"F2.wireOp",EDGE,"E6"),sQuery(id+"F2.wireOp",EDGE,"E16")])]});
            var Q23;
            Q23=makeQuery(id+"F3.opExtrude","CAP_EDGE",EDGE,{"disambiguationData":[OSD([sQuery(id+"F2.wireOp",EDGE,"E3"),sQuery(id+"F2.wireOp",EDGE,"E4.MirrorCS"),sQuery(id+"F2.wireOp",EDGE,"E17")])],"isStart":false});
            var Q24;
            Q24=makeQuery(id+"F3.opExtrude","CAP_EDGE",EDGE,{"disambiguationData":[OSD([sQuery(id+"F2.wireOp",EDGE,"E3"),sQuery(id+"F2.wireOp",EDGE,"E4.MirrorCS"),sQuery(id+"F2.wireOp",EDGE,"E17")])],"isStart":true});
            var Q25;
            Q25=makeQuery(id+"F3.opExtrude","SWEPT_EDGE",EDGE,{"disambiguationData":[OSD([sQuery(id+"F2.wireOp",EDGE,"E4.MirrorCS"),sQuery(id+"F2.wireOp",EDGE,"E8")])]});
            var Q26;
            Q26=makeQuery(id+"F3.opExtrude","SWEPT_EDGE",EDGE,{"disambiguationData":[OSD([sQuery(id+"F2.wireOp",EDGE,"E16"),sQuery(id+"F2.wireOp",EDGE,"E17")])]});
            var Q27;
            Q27=makeQuery(id+"F6.opChamfer","BLEND_EDGE",EDGE,{"blendedFrom":[makeQuery(id+"F3.opExtrude","CAP_EDGE",EDGE,{"disambiguationData":[OSD([sQuery(id+"F2.wireOp",EDGE,"E15.bottom")])],"isStart":false}),makeQuery(id+"F3.opExtrude","SWEPT_FACE",FACE,{"disambiguationData":[OSD([sQuery(id+"F2.wireOp",EDGE,"E22")])]})],"blendedInto":[makeQuery(id+"F3.opExtrude","SWEPT_FACE",FACE,{"disambiguationData":[OSD([sQuery(id+"F2.wireOp",EDGE,"E22")])]})]});
            var Q28;
            Q28=makeQuery(id+"F6.opChamfer","BLEND_EDGE",EDGE,{"blendedFrom":[makeQuery(id+"F3.opExtrude","CAP_EDGE",EDGE,{"disambiguationData":[OSD([sQuery(id+"F2.wireOp",EDGE,"E15.bottom")])],"isStart":true}),makeQuery(id+"F3.opExtrude","SWEPT_FACE",FACE,{"disambiguationData":[OSD([sQuery(id+"F2.wireOp",EDGE,"E22")])]})],"blendedInto":[makeQuery(id+"F3.opExtrude","SWEPT_FACE",FACE,{"disambiguationData":[OSD([sQuery(id+"F2.wireOp",EDGE,"E22")])]})]});
            var Q29;
            {var subQ0=sQuery(id+"F2.wireOp",EDGE,"E8");var subQ1=sQuery(id+"F2.wireOp",EDGE,"E4.MirrorCS");Q29=makeQuery(id+"F7.opChamfer","BLEND_EDGE",EDGE,{"blendedFrom":[makeQuery(id+"F3.opExtrude","SWEPT_EDGE",EDGE,{"disambiguationData":[OSD([subQ1,subQ0])]}),makeQuery(id+"F3.opExtrude","CAP_FACE",FACE,{"disambiguationData":[OSD([sQuery(id+"F2.wireOp",EDGE,"E3"),subQ1,sQuery(id+"F2.wireOp",EDGE,"E6"),sQuery(id+"F2.wireOp",EDGE,"E7"),subQ0,sQuery(id+"F2.wireOp",EDGE,"E9"),sQuery(id+"F2.wireOp",EDGE,"E11"),sQuery(id+"F2.wireOp",EDGE,"E12"),sQuery(id+"F2.wireOp",EDGE,"E15.bottom"),sQuery(id+"F2.wireOp",EDGE,"E15.left"),sQuery(id+"F2.wireOp",EDGE,"E15.right"),sQuery(id+"F2.wireOp",EDGE,"E16"),sQuery(id+"F2.wireOp",EDGE,"E17"),sQuery(id+"F2.wireOp",EDGE,"E19.0"),sQuery(id+"F2.wireOp",EDGE,"E22"),sQuery(id+"F2.wireOp",EDGE,"E23.0"),sQuery(id+"F2.wireOp",EDGE,"E24.0"),sQuery(id+"F2.wireOp",EDGE,"E24.1"),sQuery(id+"F2.wireOp",EDGE,"E25"),sQuery(id+"F2.wireOp",EDGE,"E26"),sQuery(id+"F2.wireOp",EDGE,"E27"),sQuery(id+"F2.wireOp",EDGE,"E28"),sQuery(id+"F2.wireOp",EDGE,"E29")])],"isStart":false})],"blendedInto":[makeQuery(id+"F3.opExtrude","CAP_FACE",FACE,{"disambiguationData":[OSD([sQuery(id+"F2.wireOp",EDGE,"E3"),subQ1,sQuery(id+"F2.wireOp",EDGE,"E6"),sQuery(id+"F2.wireOp",EDGE,"E7"),subQ0,sQuery(id+"F2.wireOp",EDGE,"E9"),sQuery(id+"F2.wireOp",EDGE,"E11"),sQuery(id+"F2.wireOp",EDGE,"E12"),sQuery(id+"F2.wireOp",EDGE,"E15.bottom"),sQuery(id+"F2.wireOp",EDGE,"E15.left"),sQuery(id+"F2.wireOp",EDGE,"E15.right"),sQuery(id+"F2.wireOp",EDGE,"E16"),sQuery(id+"F2.wireOp",EDGE,"E17"),sQuery(id+"F2.wireOp",EDGE,"E19.0"),sQuery(id+"F2.wireOp",EDGE,"E22"),sQuery(id+"F2.wireOp",EDGE,"E23.0"),sQuery(id+"F2.wireOp",EDGE,"E24.0"),sQuery(id+"F2.wireOp",EDGE,"E24.1"),sQuery(id+"F2.wireOp",EDGE,"E25"),sQuery(id+"F2.wireOp",EDGE,"E26"),sQuery(id+"F2.wireOp",EDGE,"E27"),sQuery(id+"F2.wireOp",EDGE,"E28"),sQuery(id+"F2.wireOp",EDGE,"E29")])],"isStart":false})]});}
            var Q30;
            {var subQ0=sQuery(id+"F2.wireOp",EDGE,"E8");var subQ1=sQuery(id+"F2.wireOp",EDGE,"E4.MirrorCS");Q30=makeQuery(id+"F7.opChamfer","BLEND_EDGE",EDGE,{"blendedFrom":[makeQuery(id+"F3.opExtrude","SWEPT_EDGE",EDGE,{"disambiguationData":[OSD([subQ1,subQ0])]}),makeQuery(id+"F3.opExtrude","CAP_FACE",FACE,{"disambiguationData":[OSD([sQuery(id+"F2.wireOp",EDGE,"E3"),subQ1,sQuery(id+"F2.wireOp",EDGE,"E6"),sQuery(id+"F2.wireOp",EDGE,"E7"),subQ0,sQuery(id+"F2.wireOp",EDGE,"E9"),sQuery(id+"F2.wireOp",EDGE,"E11"),sQuery(id+"F2.wireOp",EDGE,"E12"),sQuery(id+"F2.wireOp",EDGE,"E15.bottom"),sQuery(id+"F2.wireOp",EDGE,"E15.left"),sQuery(id+"F2.wireOp",EDGE,"E15.right"),sQuery(id+"F2.wireOp",EDGE,"E16"),sQuery(id+"F2.wireOp",EDGE,"E17"),sQuery(id+"F2.wireOp",EDGE,"E19.0"),sQuery(id+"F2.wireOp",EDGE,"E22"),sQuery(id+"F2.wireOp",EDGE,"E23.0"),sQuery(id+"F2.wireOp",EDGE,"E24.0"),sQuery(id+"F2.wireOp",EDGE,"E24.1"),sQuery(id+"F2.wireOp",EDGE,"E25"),sQuery(id+"F2.wireOp",EDGE,"E26"),sQuery(id+"F2.wireOp",EDGE,"E27"),sQuery(id+"F2.wireOp",EDGE,"E28"),sQuery(id+"F2.wireOp",EDGE,"E29")])],"isStart":true})],"blendedInto":[makeQuery(id+"F3.opExtrude","CAP_FACE",FACE,{"disambiguationData":[OSD([sQuery(id+"F2.wireOp",EDGE,"E3"),subQ1,sQuery(id+"F2.wireOp",EDGE,"E6"),sQuery(id+"F2.wireOp",EDGE,"E7"),subQ0,sQuery(id+"F2.wireOp",EDGE,"E9"),sQuery(id+"F2.wireOp",EDGE,"E11"),sQuery(id+"F2.wireOp",EDGE,"E12"),sQuery(id+"F2.wireOp",EDGE,"E15.bottom"),sQuery(id+"F2.wireOp",EDGE,"E15.left"),sQuery(id+"F2.wireOp",EDGE,"E15.right"),sQuery(id+"F2.wireOp",EDGE,"E16"),sQuery(id+"F2.wireOp",EDGE,"E17"),sQuery(id+"F2.wireOp",EDGE,"E19.0"),sQuery(id+"F2.wireOp",EDGE,"E22"),sQuery(id+"F2.wireOp",EDGE,"E23.0"),sQuery(id+"F2.wireOp",EDGE,"E24.0"),sQuery(id+"F2.wireOp",EDGE,"E24.1"),sQuery(id+"F2.wireOp",EDGE,"E25"),sQuery(id+"F2.wireOp",EDGE,"E26"),sQuery(id+"F2.wireOp",EDGE,"E27"),sQuery(id+"F2.wireOp",EDGE,"E28"),sQuery(id+"F2.wireOp",EDGE,"E29")])],"isStart":true})]});}
            chamfer(context, id + "F15", {"entities" : qUnion([Q0, Q1, Q2, Q3, Q4, Q5, Q6, Q7, Q8, Q9, Q10, Q11, Q12, Q13, Q14, Q15, Q16, Q17, Q18, Q19, Q20, Q21, Q22, Q23, Q24, Q25, Q26, Q27, Q28, Q29, Q30]), "width" : .5 * mm, "tangentPropagation" : true});
        }
        {
            var Q0;
            Q0=qCreatedBy(makeId("Right.planeOp"),FACE);
            cPlane(context, id + "F16", {"entities" : qUnion([Q0]), "cplaneType" : CPlaneType.OFFSET, "offset" : 5.5 * mm, "width" : 150 * mm, "height" : 150 * mm});
        }
        {
            var Q0;
            Q0=qCreatedBy(id+"F16.planeOp",FACE);
            var sketch = newSketch(context, id + "F17", { "sketchPlane" : qUnion([Q0])});
            skLineSegment(sketch, "E42", {"start": v(0, 0) * mm, "end": v(-1.5, 0) * mm});
            skLineSegment(sketch, "E43", {"start": v(-1.5, 0) * mm, "end": v(-1.5, 33.5) * mm});
            skLineSegment(sketch, "E44", {"start": v(-1.5, 33.5) * mm, "end": v(3.5, 33.5) * mm});
            skLineSegment(sketch, "E45", {"start": v(3.5, 33.5) * mm, "end": v(3.5, 0) * mm});
            skLineSegment(sketch, "E46", {"start": v(3.5, 0) * mm, "end": v(-1.5, 0) * mm});
            skLineSegment(sketch, "E47", {"start": v(-1.5, 0) * mm, "end": v(-1.5, 5.2) * mm});
            skLineSegment(sketch, "E48", {"start": v(-1.5, 5.2) * mm, "end": v(0.5, 5.2) * mm});
            skLineSegment(sketch, "E49", {"start": v(0.5, 5.2) * mm, "end": v(0.5, 32.6) * mm});
            skLineSegment(sketch, "E50", {"start": v(0.5, 32.6) * mm, "end": v(-1.5, 32.6) * mm});
            skLineSegment(sketch, "E51.MirrorCS", {"start": v(-3.5, 32.6) * mm, "end": v(-1.5, 32.6) * mm});
            skLineSegment(sketch, "E52.MirrorCS", {"start": v(-1.5, 33.5) * mm, "end": v(-6.5, 33.5) * mm});
            skLineSegment(sketch, "E53.MirrorCS", {"start": v(-6.5, 33.5) * mm, "end": v(-6.5, 0) * mm});
            skLineSegment(sketch, "E54", {"start": v(-6.5, 0) * mm, "end": v(-6.5, 11.1) * mm});
            skLineSegment(sketch, "E55", {"start": v(-6.5, 11.1) * mm, "end": v(-1.5, 11.1) * mm});
            skLineSegment(sketch, "E56", {"start": v(-1.5, 11.1) * mm, "end": v(-1.5, 7.7) * mm});
            skLineSegment(sketch, "E57", {"start": v(-1.5, 7.7) * mm, "end": v(-6.5, 7.7) * mm});
            skLineSegment(sketch, "E58", {"start": v(-3.5, 32.6) * mm, "end": v(-3.5, 11.1) * mm});
            skPoint(sketch, "E58.endSnap0", {"position": v(-4, 11.1) * mm});
            skLineSegment(sketch, "E59", {"start": v(3.5, 0) * mm, "end": v(3.5, 1.8) * mm});
            skLineSegment(sketch, "E60", {"start": v(3.5, 1.8) * mm, "end": v(-1.5, 1.8) * mm});
            skLineSegment(sketch, "E61", {"start": v(-1.5, 5.2) * mm, "end": v(-2.5, 5.2) * mm});
            skLineSegment(sketch, "E62.bottom", {"start": v(-2.5, 5.2) * mm, "end": v(-1.5, 5.2) * mm});
            skLineSegment(sketch, "E62.top", {"start": v(-2.5, 1.8) * mm, "end": v(-1.5, 1.8) * mm});
            skLineSegment(sketch, "E62.left", {"start": v(-2.5, 5.2) * mm, "end": v(-2.5, 1.8) * mm});
            skLineSegment(sketch, "E62.right", {"start": v(-1.5, 5.2) * mm, "end": v(-1.5, 1.8) * mm});
            skLineSegment(sketch, "E63", {"start": v(-1.5, 7.7) * mm, "end": v(-0.5, 7.7) * mm});
            skLineSegment(sketch, "E64.bottom", {"start": v(-0.5, 7.7) * mm, "end": v(-1.5, 7.7) * mm});
            skLineSegment(sketch, "E64.top", {"start": v(-0.5, 11.1) * mm, "end": v(-1.5, 11.1) * mm});
            skLineSegment(sketch, "E64.left", {"start": v(-0.5, 7.7) * mm, "end": v(-0.5, 11.1) * mm});
            skLineSegment(sketch, "E64.right", {"start": v(-1.5, 7.7) * mm, "end": v(-1.5, 11.1) * mm});
            skLineSegment(sketch, "E65", {"start": v(0.5, 32.6) * mm, "end": v(1.8, 32.6) * mm});
            skLineSegment(sketch, "E66", {"start": v(1.8, 32.6) * mm, "end": v(1.8, 31.1) * mm});
            skLineSegment(sketch, "E67", {"start": v(1.8, 31.1) * mm, "end": v(0.5, 29.8) * mm});
            skLineSegment(sketch, "E68.MirrorCS", {"start": v(-3.5, 32.6) * mm, "end": v(-4.8, 32.6) * mm});
            skLineSegment(sketch, "E69.MirrorCS", {"start": v(-4.8, 32.6) * mm, "end": v(-4.8, 31.1) * mm});
            skLineSegment(sketch, "E70.MirrorCS", {"start": v(-4.8, 31.1) * mm, "end": v(-3.5, 29.8) * mm});
            skSolve(sketch);
        }
        {
            var Q0;
            {var subQ0=sQuery(id+"F17.wireOp",EDGE,"E53.MirrorCS");Q0=makeQuery(id+"F17.imprint","IMPRINT",FACE,{"disambiguationData":[TD([[makeQuery(id+"F17.imprint","IMPRINT",EDGE,{"derivedFrom":subQ0}),1.0]])]});}
            var Q1;
            {var subQ0=sQuery(id+"F17.wireOp",EDGE,"E56");Q1=makeQuery(id+"F17.imprint","IMPRINT",FACE,{"disambiguationData":[TD([[makeQuery(id+"F17.imprint","IMPRINT",EDGE,{"derivedFrom":subQ0}),-1.0]])]});}
            var Q2;
            Q2=makeQuery(id+"F17.imprint","IMPRINT",FACE,{"disambiguationData":[TD([[makeQuery(id+"F17.imprint","IMPRINT",EDGE,{"derivedFrom":sQuery(id+"F17.wireOp",EDGE,"E44")}),-1.0]])]});
            var Q3;
            {var subQ0=sQuery(id+"F17.wireOp",EDGE,"E57");Q3=makeQuery(id+"F17.imprint","IMPRINT",FACE,{"disambiguationData":[TD([[makeQuery(id+"F17.imprint","IMPRINT",EDGE,{"derivedFrom":subQ0}),-1.0]])]});}
            var Q4;
            Q4=makeQuery(id+"F17.imprint","IMPRINT",FACE,{"disambiguationData":[TD([[makeQuery(id+"F17.imprint","IMPRINT",EDGE,{"derivedFrom":sQuery(id+"F17.wireOp",EDGE,"E62.bottom")}),-1.0]])]});
            var Q5;
            Q5=makeQuery(id+"F17.imprint","IMPRINT",FACE,{"disambiguationData":[TD([[makeQuery(id+"F17.imprint","IMPRINT",EDGE,{"derivedFrom":sQuery(id+"F17.wireOp",EDGE,"E64.bottom")}),-1.0]])]});
            extrude(context, id + "F18", {"entities" : qUnion([Q0, Q1, Q2, Q3, Q4, Q5]), "depth" : 1.3 * mm, "offsetDistance" : 25 * mm});
        }
        {
            var Q0;
            Q0=makeQuery(id+"F18.opExtrude","SWEPT_EDGE",EDGE,{"disambiguationData":[OSD([sQuery(id+"F17.wireOp",EDGE,"E52.MirrorCS"),sQuery(id+"F17.wireOp",EDGE,"E53.MirrorCS")])]});
            var Q1;
            Q1=makeQuery(id+"F18.opExtrude","SWEPT_EDGE",EDGE,{"disambiguationData":[OSD([sQuery(id+"F17.wireOp",EDGE,"E44"),sQuery(id+"F17.wireOp",EDGE,"E45")])]});
            var Q2;
            Q2=makeQuery(id+"F18.opExtrude","SWEPT_EDGE",EDGE,{"disambiguationData":[OSD([sQuery(id+"F17.wireOp",EDGE,"E54"),sQuery(id+"F17.wireOp",EDGE,"E57")])]});
            var Q3;
            Q3=makeQuery(id+"F18.opExtrude","SWEPT_EDGE",EDGE,{"disambiguationData":[OSD([sQuery(id+"F17.wireOp",EDGE,"E45"),sQuery(id+"F17.wireOp",EDGE,"E59"),sQuery(id+"F17.wireOp",EDGE,"E60")])]});
            chamfer(context, id + "F19", {"entities" : qUnion([Q0, Q1, Q2, Q3]), "width" : 1.6 * mm, "tangentPropagation" : true});
        }
        {
            var Q0;
            Q0=makeQuery(id+"F18.opExtrude","SWEPT_EDGE",EDGE,{"disambiguationData":[OSD([sQuery(id+"F17.wireOp",EDGE,"E68.MirrorCS"),sQuery(id+"F17.wireOp",EDGE,"E69.MirrorCS")])]});
            var Q1;
            Q1=makeQuery(id+"F18.opExtrude","SWEPT_EDGE",EDGE,{"disambiguationData":[OSD([sQuery(id+"F17.wireOp",EDGE,"E69.MirrorCS"),sQuery(id+"F17.wireOp",EDGE,"E70.MirrorCS")])]});
            var Q2;
            Q2=makeQuery(id+"F18.opExtrude","SWEPT_EDGE",EDGE,{"disambiguationData":[OSD([sQuery(id+"F17.wireOp",EDGE,"E58"),sQuery(id+"F17.wireOp",EDGE,"E70.MirrorCS")])]});
            var Q3;
            Q3=makeQuery(id+"F18.opExtrude","SWEPT_EDGE",EDGE,{"disambiguationData":[OSD([sQuery(id+"F17.wireOp",EDGE,"E49"),sQuery(id+"F17.wireOp",EDGE,"E67")])]});
            var Q4;
            Q4=makeQuery(id+"F18.opExtrude","SWEPT_EDGE",EDGE,{"disambiguationData":[OSD([sQuery(id+"F17.wireOp",EDGE,"E65"),sQuery(id+"F17.wireOp",EDGE,"E66")])]});
            var Q5;
            Q5=makeQuery(id+"F18.opExtrude","SWEPT_EDGE",EDGE,{"disambiguationData":[OSD([sQuery(id+"F17.wireOp",EDGE,"E66"),sQuery(id+"F17.wireOp",EDGE,"E67")])]});
            chamfer(context, id + "F20", {"entities" : qUnion([Q0, Q1, Q2, Q3, Q4, Q5]), "width" : .6 * mm, "tangentPropagation" : true});
        }
        {
            var Q0;
            Q0=makeQuery(id+"F3.opExtrude","SWEPT_BODY",BODY,{"disambiguationData":[OSD([sQuery(id+"F2.wireOp",EDGE,"E3"),sQuery(id+"F2.wireOp",EDGE,"E4.MirrorCS"),sQuery(id+"F2.wireOp",EDGE,"E5"),sQuery(id+"F2.wireOp",EDGE,"E6"),sQuery(id+"F2.wireOp",EDGE,"E7"),sQuery(id+"F2.wireOp",EDGE,"E8"),sQuery(id+"F2.wireOp",EDGE,"E9"),sQuery(id+"F2.wireOp",EDGE,"E11"),sQuery(id+"F2.wireOp",EDGE,"E12"),sQuery(id+"F2.wireOp",EDGE,"0akQF3o6-GRSy-sqst-GOAi-R7572j4TWCA9"),sQuery(id+"F2.wireOp",EDGE,"Rr7SK3JZ-Egbp-8AZP-2McZ-Qu5wQ8jnj7ba"),sQuery(id+"F2.wireOp",EDGE,"E15.bottom"),sQuery(id+"F2.wireOp",EDGE,"E15.left"),sQuery(id+"F2.wireOp",EDGE,"E15.right"),sQuery(id+"F2.wireOp",EDGE,"UHZCBOe5-mY96-04BQ-GKVw-0XouIqEKjYRg")])]});
            var Q1;
            Q1=makeQuery(id+"F18.opExtrude","SWEPT_BODY",BODY,{"disambiguationData":[OSD([sQuery(id+"F17.wireOp",EDGE,"E44"),sQuery(id+"F17.wireOp",EDGE,"E45"),sQuery(id+"F17.wireOp",EDGE,"E47"),sQuery(id+"F17.wireOp",EDGE,"E48"),sQuery(id+"F17.wireOp",EDGE,"E49"),sQuery(id+"F17.wireOp",EDGE,"E50"),sQuery(id+"F17.wireOp",EDGE,"E51.MirrorCS"),sQuery(id+"F17.wireOp",EDGE,"E52.MirrorCS"),sQuery(id+"F17.wireOp",EDGE,"E53.MirrorCS"),sQuery(id+"F17.wireOp",EDGE,"E54"),sQuery(id+"F17.wireOp",EDGE,"E55"),sQuery(id+"F17.wireOp",EDGE,"E56"),sQuery(id+"F17.wireOp",EDGE,"E57"),sQuery(id+"F17.wireOp",EDGE,"E58"),sQuery(id+"F17.wireOp",EDGE,"E60")])]});
            var Q2;
            Q2=sQuery(id+"F0.wireOp",EDGE,"E1.bottom");
            transform(context, id + "F21", {"entities" : qUnion([Q0, Q1]), "transformType" : TransformType.ROTATION, "transformAxis" : qUnion([Q2]), "angle" : 90 * degree, "oppositeDirection" : true, "makeCopy" : false});
        }
        {
            var Q0;
            Q0=makeQuery(id+"F18.opExtrude","SWEPT_BODY",BODY,{"disambiguationData":[OSD([sQuery(id+"F17.wireOp",EDGE,"E44"),sQuery(id+"F17.wireOp",EDGE,"E45"),sQuery(id+"F17.wireOp",EDGE,"E48"),sQuery(id+"F17.wireOp",EDGE,"E49"),sQuery(id+"F17.wireOp",EDGE,"E50"),sQuery(id+"F17.wireOp",EDGE,"E51.MirrorCS"),sQuery(id+"F17.wireOp",EDGE,"E52.MirrorCS"),sQuery(id+"F17.wireOp",EDGE,"E53.MirrorCS"),sQuery(id+"F17.wireOp",EDGE,"E54"),sQuery(id+"F17.wireOp",EDGE,"E55"),sQuery(id+"F17.wireOp",EDGE,"E57"),sQuery(id+"F17.wireOp",EDGE,"E58"),sQuery(id+"F17.wireOp",EDGE,"E60"),sQuery(id+"F17.wireOp",EDGE,"E62.bottom"),sQuery(id+"F17.wireOp",EDGE,"E62.top"),sQuery(id+"F17.wireOp",EDGE,"E62.left"),sQuery(id+"F17.wireOp",EDGE,"E64.bottom"),sQuery(id+"F17.wireOp",EDGE,"E64.top"),sQuery(id+"F17.wireOp",EDGE,"E64.left"),sQuery(id+"F17.wireOp",EDGE,"E65"),sQuery(id+"F17.wireOp",EDGE,"E66"),sQuery(id+"F17.wireOp",EDGE,"E67"),sQuery(id+"F17.wireOp",EDGE,"E68.MirrorCS"),sQuery(id+"F17.wireOp",EDGE,"E69.MirrorCS"),sQuery(id+"F17.wireOp",EDGE,"E70.MirrorCS")])]});
            var Q1;
            {var subQ0=sQuery(id+"F13.wireOp",EDGE,"E41.right");Q1=makeQuery(id+"F15.opChamfer","BLEND_EDGE",EDGE,{"blendedFrom":[makeQuery(id+"F14.boolean.opBoolean","COPY",EDGE,{"derivedFrom":makeQuery(id+"F14.opExtrude","CAP_EDGE",EDGE,{"disambiguationData":[OSD([subQ0])],"isStart":false})}),makeQuery(id+"F14.boolean.opBoolean","COPY",FACE,{"derivedFrom":makeQuery(id+"F14.opExtrude","CAP_FACE",FACE,{"disambiguationData":[OSD([sQuery(id+"F13.wireOp",EDGE,"E41.bottom"),sQuery(id+"F13.wireOp",EDGE,"E41.top"),sQuery(id+"F13.wireOp",EDGE,"E41.left"),subQ0])],"isStart":false})})],"blendedInto":[makeQuery(id+"F14.boolean.opBoolean","COPY",FACE,{"derivedFrom":makeQuery(id+"F14.opExtrude","CAP_FACE",FACE,{"disambiguationData":[OSD([sQuery(id+"F13.wireOp",EDGE,"E41.bottom"),sQuery(id+"F13.wireOp",EDGE,"E41.top"),sQuery(id+"F13.wireOp",EDGE,"E41.left"),subQ0])],"isStart":false})})]});}
            transform(context, id + "F22", {"entities" : qUnion([Q0]), "transformType" : TransformType.ROTATION, "transformAxis" : qUnion([Q1]), "angle" : 90 * degree, "makeCopy" : false});
        }
    });
